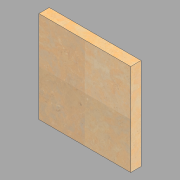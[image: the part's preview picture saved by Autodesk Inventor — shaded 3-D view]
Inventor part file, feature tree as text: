
AUTODESK INVENTOR PART (.ipt)
format: ipt  version: 2022.1 (Build 261234020, 234B)  size: 103,936 bytes
history: native  units: in
note: dims shown in document units (in); Inventor stores cm internally (conversion verified against a paired STEP export)
features: extrude x1, sketch x1
ambient origin geometry x8: Origin, YZ Plane, XZ Plane, XY Plane, X Axis, Y Axis, Z Axis, Center Point
bodies: Solid1 (feature_tree)
feature tree (2):
  extrude  "Extrusion1"  Depth=17.625in
  sketch  "Sketch1"  dims[d0=17.625in d1=17.625in d2=2.0in d3=0.0in]
